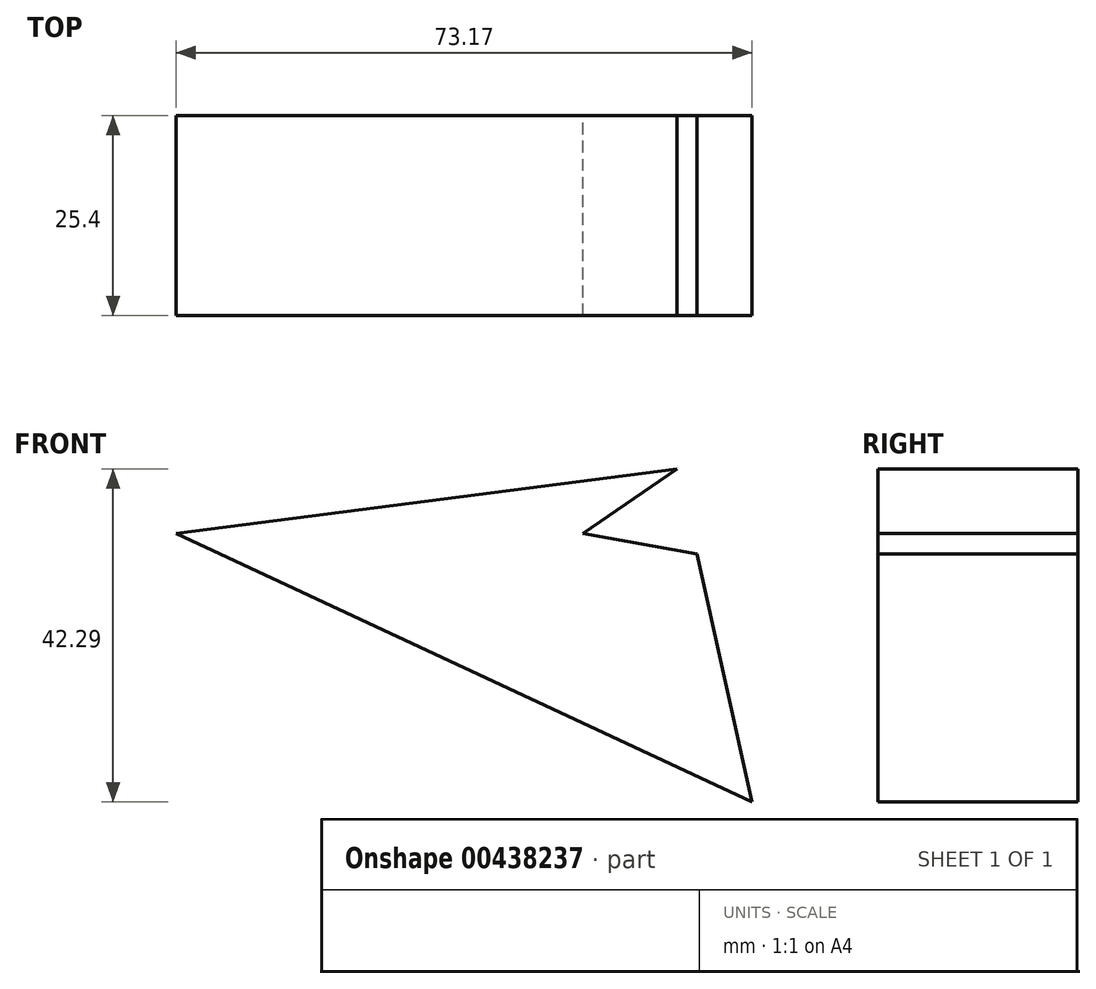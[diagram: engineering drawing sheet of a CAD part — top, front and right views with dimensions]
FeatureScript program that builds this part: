
annotation { "Feature Type Name" : "Feature", "Feature Type Description" : "" }
export const myFeature = defineFeature(function(context is Context, id is Id, definition is map)
    precondition{}
    {
        {
            var Q0;
            Q0=qCreatedBy(makeId("Front.planeOp"),FACE);
            var sketch = newSketch(context, id + "F0", { "sketchPlane" : qUnion([Q0])});
            skLineSegment(sketch, "E0", {"start": v(-32.08, 7.17) * mm, "end": v(31.52, 15.37) * mm});
            skLineSegment(sketch, "E1", {"start": v(34.07, 4.59) * mm, "end": v(41.09, -26.92) * mm});
            skLineSegment(sketch, "E2", {"start": v(-32.08, 7.17) * mm, "end": v(41.09, -26.92) * mm});
            skLineSegment(sketch, "E3", {"start": v(31.52, 15.37) * mm, "end": v(19.6, 7.17) * mm});
            skLineSegment(sketch, "E4", {"start": v(19.6, 7.17) * mm, "end": v(34.07, 4.59) * mm});
            skSolve(sketch);
        }
        {
            var Q0;
            Q0=makeQuery(id+"F0.imprint","IMPRINT",FACE,{"disambiguationData":[TD([[makeQuery(id+"F0.imprint","IMPRINT",EDGE,{"derivedFrom":sQuery(id+"F0.wireOp",EDGE,"E0")}),-1.0]])]});
            extrude(context, id + "F1", {"entities" : qUnion([Q0]), "depth" : 25.4 * mm, "offsetDistance" : 25.4 * mm});
        }
    });
